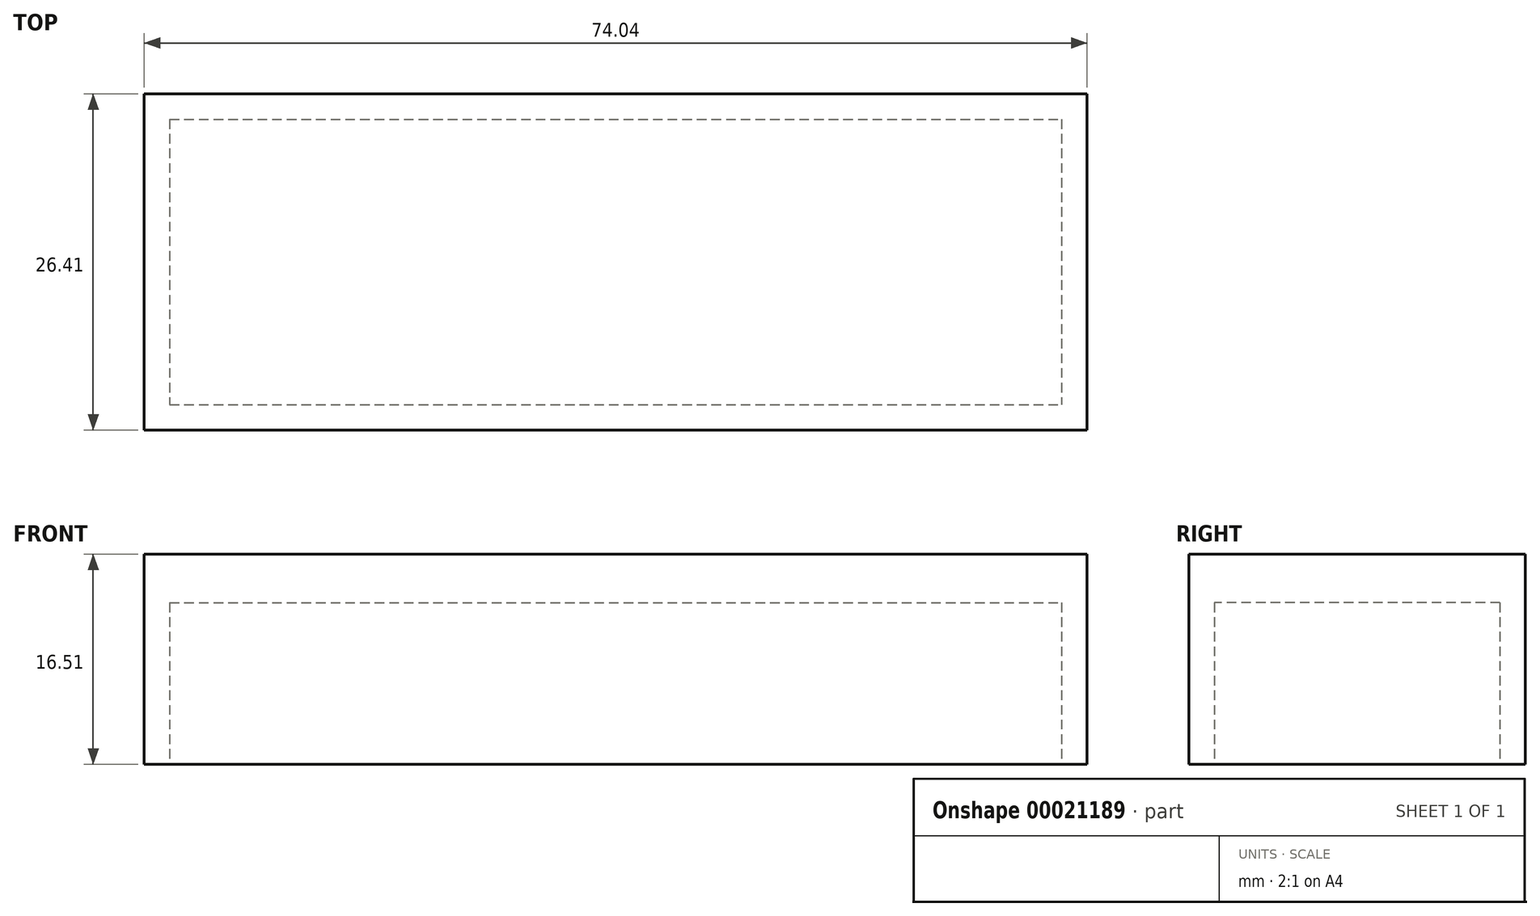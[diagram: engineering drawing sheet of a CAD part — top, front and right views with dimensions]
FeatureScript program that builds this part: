
annotation { "Feature Type Name" : "Feature", "Feature Type Description" : "" }
export const myFeature = defineFeature(function(context is Context, id is Id, definition is map)
    precondition{}
    {
        {
            var Q0;
            Q0=qCreatedBy(makeId("Top.planeOp"),FACE);
            var sketch = newSketch(context, id + "F0", { "sketchPlane" : qUnion([Q0])});
            skLineSegment(sketch, "E0.right", {"start": v(56.69, -3.29) * mm, "end": v(56.69, -29.7) * mm});
            skLineSegment(sketch, "E1", {"start": v(54.69, -27.7) * mm, "end": v(56.69, -27.7) * mm});
            skLineSegment(sketch, "E2.bottom", {"start": v(-15.35, -5.29) * mm, "end": v(54.69, -5.29) * mm});
            skLineSegment(sketch, "E0.left", {"start": v(-17.35, -3.29) * mm, "end": v(-17.35, -29.7) * mm});
            skLineSegment(sketch, "E0.top", {"start": v(-17.35, -29.7) * mm, "end": v(56.69, -29.7) * mm});
            skLineSegment(sketch, "E3", {"start": v(-17.35, -5.29) * mm, "end": v(-15.35, -5.29) * mm});
            skLineSegment(sketch, "E0.bottom", {"start": v(-17.35, -3.29) * mm, "end": v(56.69, -3.29) * mm});
            skLineSegment(sketch, "E2.right", {"start": v(54.69, -5.29) * mm, "end": v(54.69, -27.7) * mm});
            skLineSegment(sketch, "E2.top", {"start": v(-15.35, -27.7) * mm, "end": v(54.69, -27.7) * mm});
            skLineSegment(sketch, "E2.left", {"start": v(-15.35, -5.29) * mm, "end": v(-15.35, -27.7) * mm});
            skLineSegment(sketch, "E4", {"start": v(-15.35, -5.29) * mm, "end": v(-15.35, -3.29) * mm});
            skLineSegment(sketch, "E5", {"start": v(54.69, -27.7) * mm, "end": v(54.69, -29.7) * mm});
            skLineSegment(sketch, "E6", {"start": v(-15.35, -5.29) * mm, "end": v(-17.35, -5.29) * mm});
            skSolve(sketch);
        }
        {
            var Q0;
            Q0=makeQuery(id+"F0.imprint","IMPRINT",FACE,{"disambiguationData":[TD([[makeQuery(id+"F0.imprint","IMPRINT",EDGE,{"derivedFrom":sQuery(id+"F0.wireOp",EDGE,"E2.top")}),-1.0]])]});
            var Q1;
            {var subQ0=sQuery(id+"F0.wireOp",EDGE,"E4");Q1=makeQuery(id+"F0.imprint","IMPRINT",FACE,{"disambiguationData":[TD([[makeQuery(id+"F0.imprint","IMPRINT",EDGE,{"derivedFrom":subQ0}),1.0]])]});}
            var Q2;
            {var subQ4=sQuery(id+"F0.wireOp",EDGE,"E1");Q2=makeQuery(id+"F0.imprint","IMPRINT",FACE,{"disambiguationData":[TD([[makeQuery(id+"F0.imprint","IMPRINT",EDGE,{"derivedFrom":subQ4}),1.0]])]});}
            var Q3;
            {var subQ4=sQuery(id+"F0.wireOp",EDGE,"E1");Q3=makeQuery(id+"F0.imprint","IMPRINT",FACE,{"disambiguationData":[TD([[makeQuery(id+"F0.imprint","IMPRINT",EDGE,{"derivedFrom":subQ4}),-1.0]])]});}
            extrude(context, id + "F1", {"entities" : qUnion([Q0, Q1, Q2, Q3]), "depth" : 12.7 * mm});
        }
        {
            var Q0;
            Q0=makeQuery(id+"F1.opExtrude","CAP_FACE",FACE,{"disambiguationData":[OSD([sQuery(id+"F0.wireOp",EDGE,"E0.right"),sQuery(id+"F0.wireOp",EDGE,"E2.bottom"),sQuery(id+"F0.wireOp",EDGE,"E0.left"),sQuery(id+"F0.wireOp",EDGE,"E0.top"),sQuery(id+"F0.wireOp",EDGE,"E0.bottom"),sQuery(id+"F0.wireOp",EDGE,"E2.right"),sQuery(id+"F0.wireOp",EDGE,"E2.top"),sQuery(id+"F0.wireOp",EDGE,"E2.left")])],"isStart":false});
            var sketch = newSketch(context, id + "F2", { "sketchPlane" : qUnion([Q0])});
            skLineSegment(sketch, "E7.bottom", {"start": v(-17.35, -3.29) * mm, "end": v(56.69, -3.29) * mm});
            skLineSegment(sketch, "E7.top", {"start": v(-17.35, -29.7) * mm, "end": v(56.69, -29.7) * mm});
            skLineSegment(sketch, "E7.left", {"start": v(-17.35, -3.29) * mm, "end": v(-17.35, -29.7) * mm});
            skLineSegment(sketch, "E7.right", {"start": v(56.69, -3.29) * mm, "end": v(56.69, -29.7) * mm});
            skSolve(sketch);
        }
        {
            var Q0;
            Q0=makeQuery(id+"F2.imprint","IMPRINT",FACE,{"disambiguationData":[TD([[makeQuery(id+"F2.imprint","IMPRINT",EDGE,{"derivedFrom":makeQuery(id+"F1.opExtrude","CAP_EDGE",EDGE,{"disambiguationData":[OSD([sQuery(id+"F0.wireOp",EDGE,"E2.bottom")])],"isStart":false})}),-1.0]])]});
            var Q1;
            Q1=makeQuery(id+"F2.imprint","IMPRINT",FACE,{"disambiguationData":[TD([[makeQuery(id+"F2.imprint","IMPRINT",EDGE,{"derivedFrom":sQuery(id+"F2.wireOp",EDGE,"E7.bottom")}),-1.0]])]});
            extrude(context, id + "F3", {"entities" : qUnion([Q0, Q1]), "operationType" : NewBodyOperationType.ADD, "depth" : 3.8 * mm});
        }
    });
